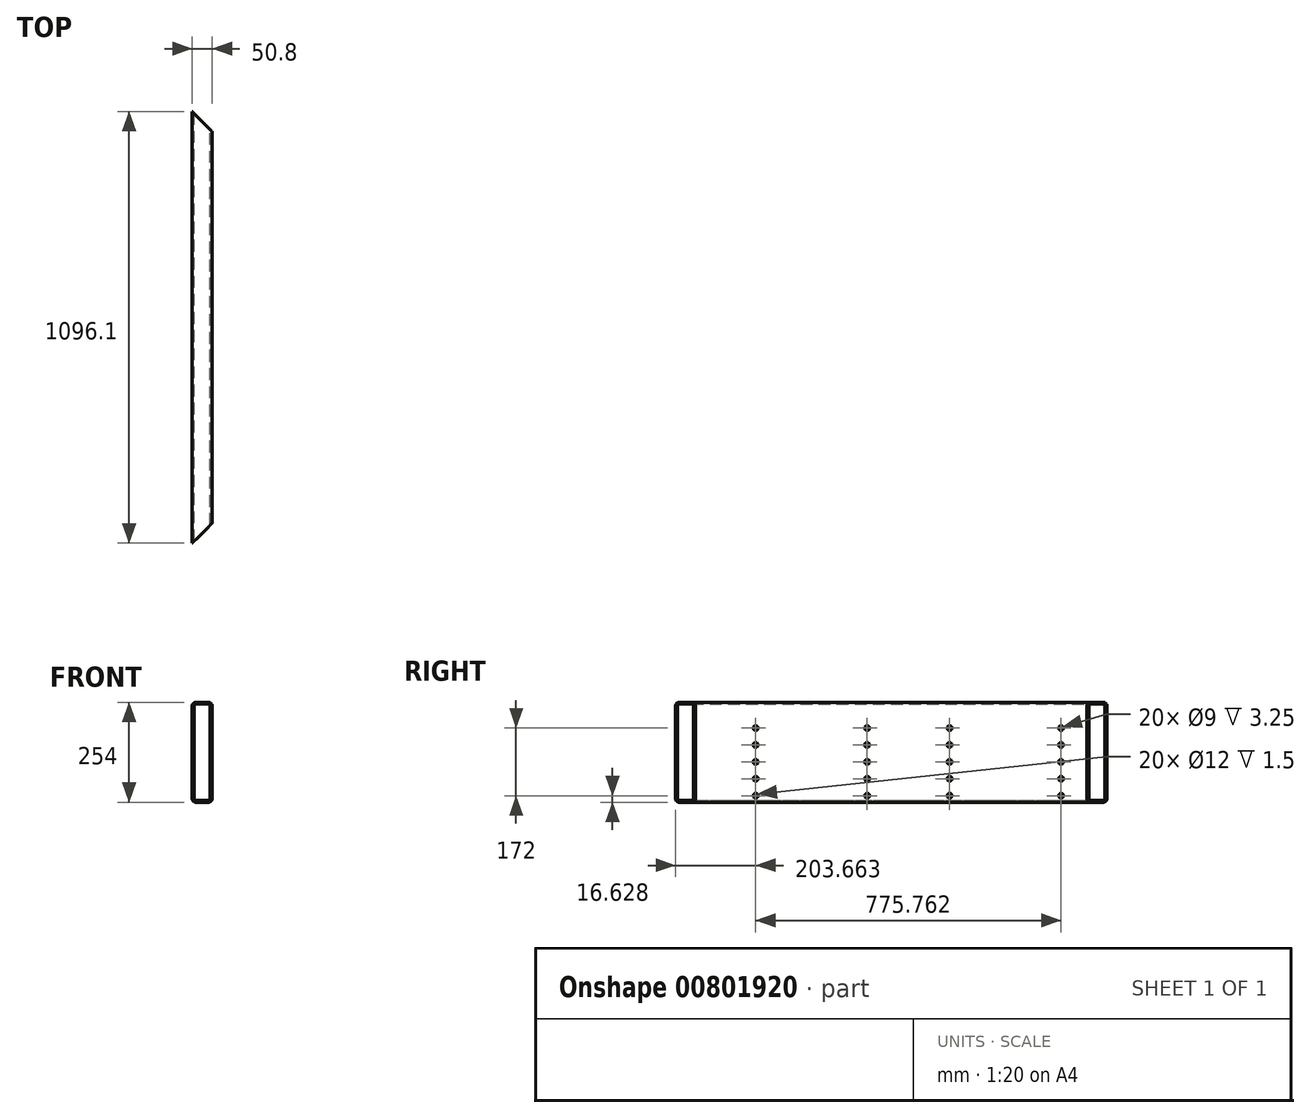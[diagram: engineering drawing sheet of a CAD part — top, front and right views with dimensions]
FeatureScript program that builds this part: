
annotation { "Feature Type Name" : "Feature", "Feature Type Description" : "" }
export const myFeature = defineFeature(function(context is Context, id is Id, definition is map)
    precondition{}
    {
        {
            var Q0;
            Q0=qCreatedBy(makeId("Front.planeOp"),FACE);
            var sketch = newSketch(context, id + "F0", { "sketchPlane" : qUnion([Q0])});
            skLineSegment(sketch, "E0.bottom", {"start": v(-9.52, 0) * mm, "end": v(-41.28, 0) * mm});
            skLineSegment(sketch, "E0.top", {"start": v(-9.53, 254) * mm, "end": v(-41.28, 254) * mm});
            skLineSegment(sketch, "E0.left", {"start": v(0, 9.53) * mm, "end": v(0, 244.47) * mm});
            skLineSegment(sketch, "E0.right", {"start": v(-50.8, 9.52) * mm, "end": v(-50.8, 244.47) * mm});
            skLineSegment(sketch, "E1.bottom", {"start": v(-41.3, 249.25) * mm, "end": v(-9.5, 249.25) * mm});
            skLineSegment(sketch, "E1.top", {"start": v(-41.3, 4.75) * mm, "end": v(-9.5, 4.75) * mm});
            skLineSegment(sketch, "E1.left", {"start": v(-46.05, 244.5) * mm, "end": v(-46.05, 9.5) * mm});
            skLineSegment(sketch, "E1.right", {"start": v(-4.75, 244.5) * mm, "end": v(-4.75, 9.5) * mm});
            skPoint(sketch, "E2.visualSharp", {"position": v(-46.05, 249.25) * mm});
            skArc(sketch, "E2.filletArc", {"start": v(-41.3, 249.25) * mm, "mid": v(-44.66, 247.86) * mm, "end": v(-46.05, 244.5) * mm});
            skPoint(sketch, "E3.visualSharp", {"position": v(-4.75, 249.25) * mm});
            skArc(sketch, "E3.filletArc", {"start": v(-4.75, 244.5) * mm, "mid": v(-6.14, 247.86) * mm, "end": v(-9.5, 249.25) * mm});
            skPoint(sketch, "E4.visualSharp", {"position": v(-4.75, 4.75) * mm});
            skArc(sketch, "E4.filletArc", {"start": v(-9.5, 4.75) * mm, "mid": v(-6.14, 6.14) * mm, "end": v(-4.75, 9.5) * mm});
            skPoint(sketch, "E5.visualSharp", {"position": v(-46.05, 4.75) * mm});
            skArc(sketch, "E5.filletArc", {"start": v(-46.05, 9.5) * mm, "mid": v(-44.66, 6.14) * mm, "end": v(-41.3, 4.75) * mm});
            skPoint(sketch, "E6.visualSharp", {"position": v(-50.8, 254) * mm});
            skArc(sketch, "E6.filletArc", {"start": v(-41.28, 254) * mm, "mid": v(-48.01, 251.21) * mm, "end": v(-50.8, 244.47) * mm});
            skPoint(sketch, "E7.visualSharp", {"position": v(0, 254) * mm});
            skArc(sketch, "E7.filletArc", {"start": v(0, 244.47) * mm, "mid": v(-2.79, 251.21) * mm, "end": v(-9.53, 254) * mm});
            skPoint(sketch, "E8.visualSharp", {"position": v(0, 0) * mm});
            skArc(sketch, "E8.filletArc", {"start": v(-9.52, 0) * mm, "mid": v(-2.79, 2.79) * mm, "end": v(0, 9.53) * mm});
            skPoint(sketch, "E9.visualSharp", {"position": v(-50.8, 0) * mm});
            skArc(sketch, "E9.filletArc", {"start": v(-50.8, 9.52) * mm, "mid": v(-48.01, 2.79) * mm, "end": v(-41.28, 0) * mm});
            skSolve(sketch);
        }
        {
            var Q0;
            Q0=qSketchRegion(id+"F0",true);
            extrude(context, id + "F1", {"entities" : qUnion([Q0]), "depth" : 1096.1 * mm});
        }
        {
            var Q0;
            Q0=makeQuery(id+"F1.opExtrude","SWEPT_FACE",FACE,{"disambiguationData":[OSD([sQuery(id+"F0.wireOp",EDGE,"E0.top")])]});
            var sketch = newSketch(context, id + "F2", { "sketchPlane" : qUnion([Q0])});
            skLineSegment(sketch, "E10", {"start": v(-50.8, 0) * mm, "end": v(0, -50.8) * mm});
            skLineSegment(sketch, "E11", {"start": v(0, -50.8) * mm, "end": v(0, 0) * mm});
            skLineSegment(sketch, "E12", {"start": v(0, 0) * mm, "end": v(-50.8, 0) * mm});
            skLineSegment(sketch, "E13", {"start": v(-50.8, -1096.1) * mm, "end": v(0, -1045.3) * mm});
            skLineSegment(sketch, "E14", {"start": v(0, -1045.3) * mm, "end": v(0, -1096.1) * mm});
            skLineSegment(sketch, "E15", {"start": v(0, -1096.1) * mm, "end": v(-50.8, -1096.1) * mm});
            skSolve(sketch);
        }
        {
            var Q0;
            Q0=qSketchRegion(id+"F2",true);
            extrude(context, id + "F3", {"entities" : qUnion([Q0]), "operationType" : NewBodyOperationType.REMOVE, "endBound" : BoundingType.THROUGH_ALL, "oppositeDirection" : true, "depth" : 25.4 * mm});
        }
        {
            var Q0;
            Q0=makeQuery(id+"F1.opExtrude","SWEPT_FACE",FACE,{"disambiguationData":[OSD([sQuery(id+"F0.wireOp",EDGE,"E0.left")])]});
            var sketch = newSketch(context, id + "F4", { "sketchPlane" : qUnion([Q0])});
            skCircle(sketch, "E16", {"center": v(-116.67, 188.63) * mm, "radius": 3.3 * mm, "construction": true});
            skCircle(sketch, "E17", {"center": v(-399.85, 188.63) * mm, "radius": 3.3 * mm, "construction": true});
            skCircle(sketch, "E18", {"center": v(-609.26, 188.63) * mm, "radius": 3.3 * mm, "construction": true});
            skCircle(sketch, "E19", {"center": v(-892.44, 188.63) * mm, "radius": 3.3 * mm, "construction": true});
            skPoint(sketch, "E20", {"position": v(-892.44, 145.63) * mm});
            skPoint(sketch, "E21", {"position": v(-892.44, 102.63) * mm});
            skPoint(sketch, "E22", {"position": v(-892.44, 59.63) * mm});
            skPoint(sketch, "E23", {"position": v(-892.44, 16.63) * mm});
            skPoint(sketch, "E24", {"position": v(-609.26, 145.63) * mm});
            skPoint(sketch, "E25", {"position": v(-609.26, 102.63) * mm});
            skPoint(sketch, "E26", {"position": v(-609.26, 59.63) * mm});
            skPoint(sketch, "E27", {"position": v(-609.26, 16.63) * mm});
            skPoint(sketch, "E28", {"position": v(-399.85, 145.63) * mm});
            skPoint(sketch, "E29", {"position": v(-399.85, 102.63) * mm});
            skPoint(sketch, "E30", {"position": v(-399.85, 59.63) * mm});
            skPoint(sketch, "E31", {"position": v(-399.85, 16.63) * mm});
            skPoint(sketch, "E32", {"position": v(-116.67, 145.63) * mm});
            skPoint(sketch, "E33", {"position": v(-116.67, 102.63) * mm});
            skPoint(sketch, "E34", {"position": v(-116.67, 59.63) * mm});
            skPoint(sketch, "E35", {"position": v(-116.67, 16.63) * mm});
            skSolve(sketch);
        }
        {
            var Q0;
            Q0=sQuery(id+"F4.wireOp",VERTEX,"E19.center");
            var Q1;
            Q1=sQuery(id+"F4.wireOp",VERTEX,"E20");
            var Q2;
            Q2=sQuery(id+"F4.wireOp",VERTEX,"E21");
            var Q3;
            Q3=sQuery(id+"F4.wireOp",VERTEX,"E22");
            var Q4;
            Q4=sQuery(id+"F4.wireOp",VERTEX,"E23");
            var Q5;
            Q5=sQuery(id+"F4.wireOp",VERTEX,"E18.center");
            var Q6;
            Q6=sQuery(id+"F4.wireOp",VERTEX,"E24");
            var Q7;
            Q7=sQuery(id+"F4.wireOp",VERTEX,"E25");
            var Q8;
            Q8=sQuery(id+"F4.wireOp",VERTEX,"E26");
            var Q9;
            Q9=sQuery(id+"F4.wireOp",VERTEX,"E27");
            var Q10;
            Q10=sQuery(id+"F4.wireOp",VERTEX,"E17.center");
            var Q11;
            Q11=sQuery(id+"F4.wireOp",VERTEX,"E28");
            var Q12;
            Q12=sQuery(id+"F4.wireOp",VERTEX,"E29");
            var Q13;
            Q13=sQuery(id+"F4.wireOp",VERTEX,"E30");
            var Q14;
            Q14=sQuery(id+"F4.wireOp",VERTEX,"E31");
            var Q15;
            Q15=sQuery(id+"F4.wireOp",VERTEX,"E16.center");
            var Q16;
            Q16=sQuery(id+"F4.wireOp",VERTEX,"E32");
            var Q17;
            Q17=sQuery(id+"F4.wireOp",VERTEX,"E33");
            var Q18;
            Q18=sQuery(id+"F4.wireOp",VERTEX,"E34");
            var Q19;
            Q19=sQuery(id+"F4.wireOp",VERTEX,"E35");
            var Q20;
            Q20=makeQuery(id+"F1.opExtrude","SWEPT_BODY",BODY,{"disambiguationData":[OSD([sQuery(id+"F0.wireOp",EDGE,"E0.bottom"),sQuery(id+"F0.wireOp",EDGE,"E0.top"),sQuery(id+"F0.wireOp",EDGE,"E0.left"),sQuery(id+"F0.wireOp",EDGE,"E0.right"),sQuery(id+"F0.wireOp",EDGE,"E1.bottom"),sQuery(id+"F0.wireOp",EDGE,"E1.top"),sQuery(id+"F0.wireOp",EDGE,"E1.left"),sQuery(id+"F0.wireOp",EDGE,"E1.right"),sQuery(id+"F0.wireOp",EDGE,"E2.filletArc"),sQuery(id+"F0.wireOp",EDGE,"E3.filletArc"),sQuery(id+"F0.wireOp",EDGE,"E4.filletArc"),sQuery(id+"F0.wireOp",EDGE,"E5.filletArc"),sQuery(id+"F0.wireOp",EDGE,"E6.filletArc"),sQuery(id+"F0.wireOp",EDGE,"E7.filletArc"),sQuery(id+"F0.wireOp",EDGE,"E8.filletArc"),sQuery(id+"F0.wireOp",EDGE,"E9.filletArc")])]});
            hole(context, id + "F5", {"style" : HoleStyle.C_BORE, "endStyle" : HoleEndStyle.BLIND, "holeDiameter" : 9 * mm, "cBoreDiameter" : 12 * mm, "cBoreDepth" : 1.5 * mm, "holeDepth" : 10 * mm, "isTappedThrough" : true, "tappedDepth" : 17 * mm, "tapClearance" : 3, "startFromSketch" : true, "locations" : qUnion([Q0, Q1, Q2, Q3, Q4, Q5, Q6, Q7, Q8, Q9, Q10, Q11, Q12, Q13, Q14, Q15, Q16, Q17, Q18, Q19]), "scope" : qUnion([Q20])});
        }
    });
